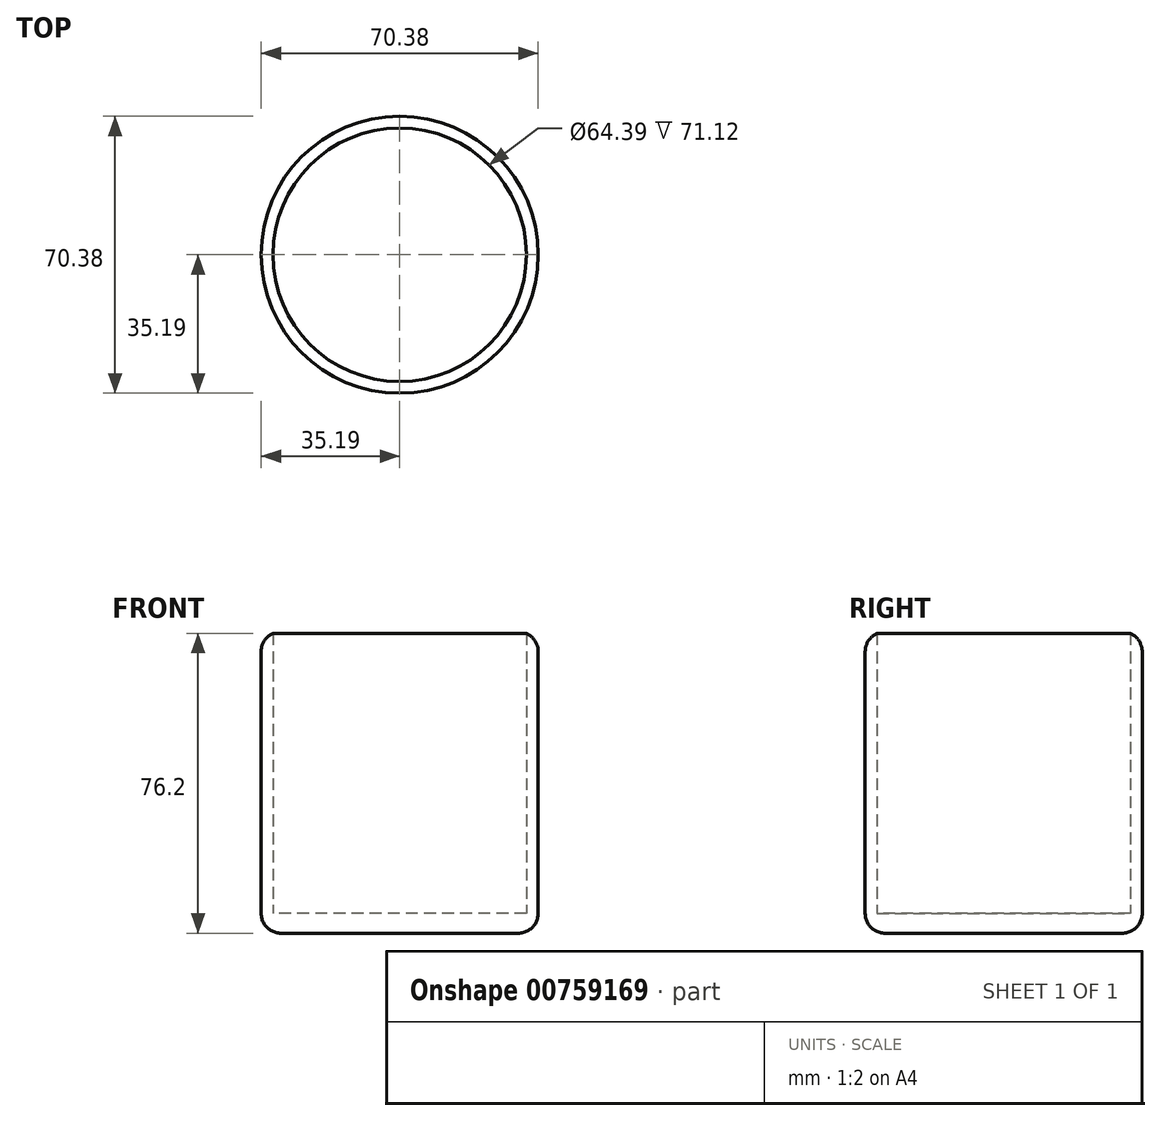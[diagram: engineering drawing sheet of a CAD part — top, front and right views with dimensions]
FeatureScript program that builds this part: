
annotation { "Feature Type Name" : "Feature", "Feature Type Description" : "" }
export const myFeature = defineFeature(function(context is Context, id is Id, definition is map)
    precondition{}
    {
        {
            var Q0;
            Q0=qCreatedBy(makeId("Top.planeOp"),FACE);
            var sketch = newSketch(context, id + "F0", { "sketchPlane" : qUnion([Q0])});
            skCircle(sketch, "E0", {"center": v(0, 0) * mm, "radius": 35.2 * mm});
            skCircle(sketch, "E1", {"center": v(0, 0) * mm, "radius": 32.2 * mm});
            skSolve(sketch);
        }
        {
            var Q0;
            Q0=makeQuery(id+"F0.imprint","IMPRINT",FACE,{"disambiguationData":[TD([[makeQuery(id+"F0.imprint","IMPRINT",EDGE,{"derivedFrom":sQuery(id+"F0.wireOp",EDGE,"E0")}),1.0]])]});
            extrude(context, id + "F1", {"entities" : qUnion([Q0]), "depth" : 76.2 * mm, "offsetDistance" : 25.4 * mm});
        }
        {
            var Q0;
            Q0=qCreatedBy(makeId("Top.planeOp"),FACE);
            var sketch = newSketch(context, id + "F2", { "sketchPlane" : qUnion([Q0])});
            skCircle(sketch, "E2", {"center": v(0, 0) * mm, "radius": 32.36 * mm});
            skSolve(sketch);
        }
        {
            var Q0;
            Q0=makeQuery(id+"F2.imprint","IMPRINT",FACE,{"disambiguationData":[TD([[makeQuery(id+"F2.imprint","IMPRINT",EDGE,{"derivedFrom":sQuery(id+"F2.wireOp",EDGE,"E2")}),1.0]])]});
            extrude(context, id + "F3", {"entities" : qUnion([Q0]), "operationType" : NewBodyOperationType.ADD, "depth" : 25.4 * mm, "offsetDistance" : 25.4 * mm});
        }
        {
            var Q0;
            Q0=makeQuery(id+"F3.opExtrude","CAP_FACE",FACE,{"disambiguationData":[OSD([sQuery(id+"F2.wireOp",EDGE,"E2")])],"isStart":false});
            extrude(context, id + "F4", {"entities" : qUnion([Q0]), "operationType" : NewBodyOperationType.REMOVE, "oppositeDirection" : true, "depth" : 20.32 * mm, "offsetDistance" : 25.4 * mm});
        }
        {
            var Q0;
            Q0=makeQuery(id+"F1.opExtrude","CAP_EDGE",EDGE,{"disambiguationData":[OSD([sQuery(id+"F0.wireOp",EDGE,"E0")])],"isStart":false});
            var Q1;
            Q1=makeQuery(id+"F1.opExtrude","CAP_EDGE",EDGE,{"disambiguationData":[OSD([sQuery(id+"F0.wireOp",EDGE,"E0")])],"isStart":true});
            fillet(context, id + "F5", {"entities" : qUnion([Q0, Q1]), "radius" : 5.08 * mm, "tangentPropagation" : true, "allowEdgeOverflow" : false});
        }
    });
